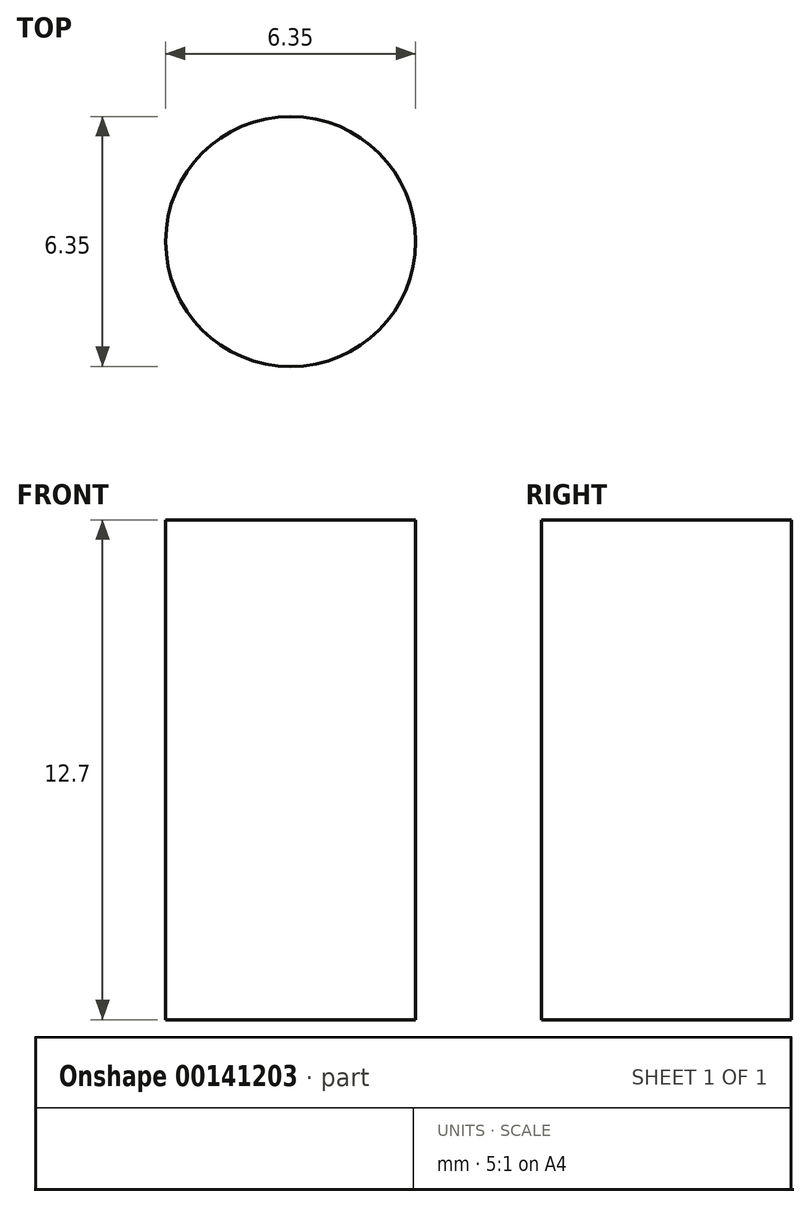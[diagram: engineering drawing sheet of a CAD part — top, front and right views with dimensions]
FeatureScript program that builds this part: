
annotation { "Feature Type Name" : "Feature", "Feature Type Description" : "" }
export const myFeature = defineFeature(function(context is Context, id is Id, definition is map)
    precondition{}
    {
        {
            var Q0;
            Q0=qCreatedBy(makeId("Top.planeOp"),FACE);
            var sketch = newSketch(context, id + "F0", { "sketchPlane" : qUnion([Q0])});
            skCircle(sketch, "E0", {"center": v(-26.31, 35.41) * mm, "radius": 3.17 * mm});
            skSolve(sketch);
        }
        {
            var Q0;
            Q0=makeQuery(id+"F0.imprint","IMPRINT",FACE,{"disambiguationData":[TD([[makeQuery(id+"F0.imprint","IMPRINT",EDGE,{"derivedFrom":sQuery(id+"F0.wireOp",EDGE,"E0")}),1.0]])]});
            extrude(context, id + "F1", {"entities" : qUnion([Q0]), "depth" : 12.7 * mm});
        }
    });
